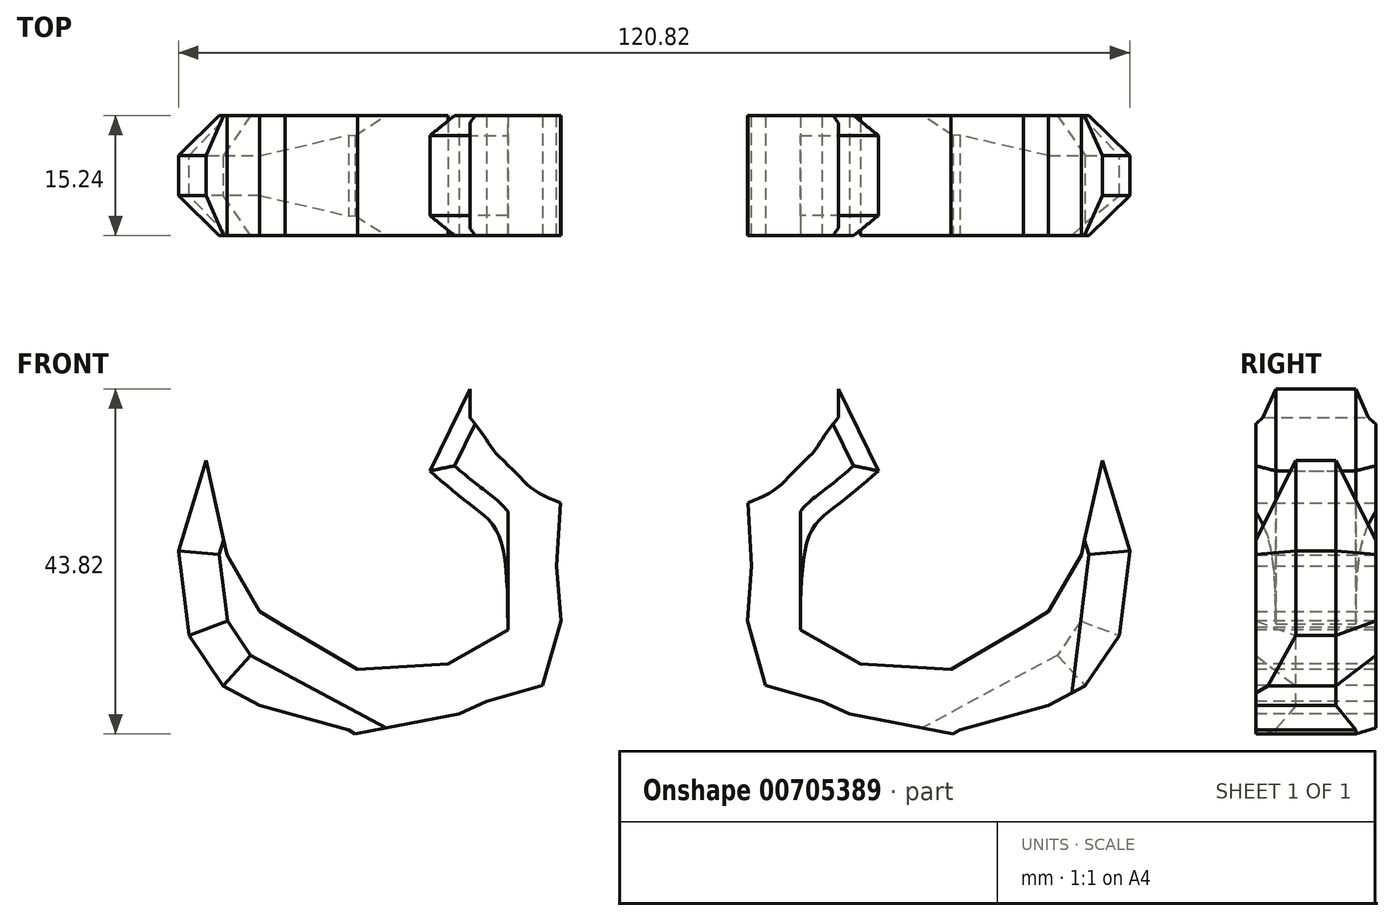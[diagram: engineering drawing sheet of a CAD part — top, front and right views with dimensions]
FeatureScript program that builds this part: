
annotation { "Feature Type Name" : "Feature", "Feature Type Description" : "" }
export const myFeature = defineFeature(function(context is Context, id is Id, definition is map)
    precondition{}
    {
        {
            var Q0;
            Q0=qCreatedBy(makeId("Front.planeOp"),FACE);
            var sketch = newSketch(context, id + "F0", { "sketchPlane" : qUnion([Q0])});
            skLineSegment(sketch, "E0", {"start": v(0, 0) * mm, "end": v(0, -3.04) * mm});
            skLineSegment(sketch, "E1", {"start": v(0, -3.04) * mm, "end": v(0, 0) * mm});
            skLineSegment(sketch, "E2", {"start": v(0, 15.49) * mm, "end": v(-8.28, 1.23) * mm});
            skLineSegment(sketch, "E3", {"start": v(-8.28, 1.23) * mm, "end": v(-12.37, 8.16) * mm});
            skLineSegment(sketch, "E4", {"start": v(-12.37, 8.16) * mm, "end": v(-11.9, 16.15) * mm});
            skFitSpline(sketch, "E5", {"points": [v(-11.9, 16.15) * mm, v(-15.37, 17.85) * mm, v(-17.68, 20.08) * mm, v(-20.4, 22.8) * mm, v(-21.58, 24.61) * mm, v(-23.4, 26.98) * mm], "startDerivative": vector(-17.13, 6.88) * mm, "endDerivative": vector(-10.36, 12.7) * mm});
            skLineSegment(sketch, "E6", {"start": v(-23.4, 26.98) * mm, "end": v(-23.4, 30.61) * mm});
            skLineSegment(sketch, "E7", {"start": v(-23.4, 30.61) * mm, "end": v(-28.49, 20.22) * mm});
            skFitSpline(sketch, "E8", {"points": [v(-28.49, 20.22) * mm, v(-23.37, 15.92) * mm, v(-19.88, 12.37) * mm, v(-18.57, 0.8) * mm], "startDerivative": vector(16.73, -14.68) * mm, "endDerivative": vector(0.35, -32.63) * mm});
            skLineSegment(sketch, "E9", {"start": v(-18.57, 0.8) * mm, "end": v(-25.11, 4.23) * mm});
            skFitSpline(sketch, "E10", {"points": [v(-25.11, 4.23) * mm, v(-32.14, 3.58) * mm, v(-37.97, 4.1) * mm, v(-37.97, 4.11) * mm, v(-37.98, 4.1) * mm], "startDerivative": vector(-12.52, -2.08) * mm, "endDerivative": vector(-0.69, -0.74) * mm});
            skLineSegment(sketch, "E11", {"start": v(-37.97, 4.11) * mm, "end": v(-43.4, 7.41) * mm});
            skLineSegment(sketch, "E12", {"start": v(-43.4, 7.41) * mm, "end": v(-46.92, 12.83) * mm});
            skLineSegment(sketch, "E13", {"start": v(-46.92, 12.83) * mm, "end": v(-48.7, 6.64) * mm});
            skLineSegment(sketch, "E14", {"start": v(-48.7, 6.64) * mm, "end": v(-46.89, 0.36) * mm});
            skLineSegment(sketch, "E15", {"start": v(-46.89, 0.36) * mm, "end": v(-50.1, 2.34) * mm});
            skLineSegment(sketch, "E16", {"start": v(-50.1, 2.34) * mm, "end": v(-54.25, 9.51) * mm});
            skLineSegment(sketch, "E17", {"start": v(-54.25, 9.51) * mm, "end": v(-56.92, 21.51) * mm});
            skLineSegment(sketch, "E18", {"start": v(-56.92, 21.51) * mm, "end": v(-60.41, 10.04) * mm});
            skLineSegment(sketch, "E19", {"start": v(-60.41, 10.04) * mm, "end": v(-59.08, -0.72) * mm});
            skLineSegment(sketch, "E20", {"start": v(-59.08, -0.72) * mm, "end": v(-61.47, 1.15) * mm});
            skLineSegment(sketch, "E21", {"start": v(-61.47, 1.15) * mm, "end": v(-65.53, 8.08) * mm});
            skLineSegment(sketch, "E22", {"start": v(-65.53, 8.08) * mm, "end": v(-66.84, 23.61) * mm});
            skLineSegment(sketch, "E23", {"start": v(-66.84, 23.61) * mm, "end": v(-70.54, 10.04) * mm});
            skLineSegment(sketch, "E24", {"start": v(-70.54, 10.04) * mm, "end": v(-70.54, -4.38) * mm});
            skLineSegment(sketch, "E25", {"start": v(-70.54, -4.38) * mm, "end": v(-64.04, -13.92) * mm});
            skLineSegment(sketch, "E26", {"start": v(-64.04, -13.92) * mm, "end": v(-58.26, -17.24) * mm});
            skLineSegment(sketch, "E27", {"start": v(-58.26, -17.24) * mm, "end": v(-57.47, -21.38) * mm});
            skLineSegment(sketch, "E28", {"start": v(-57.47, -21.38) * mm, "end": v(-50, -19.34) * mm});
            skLineSegment(sketch, "E29", {"start": v(-50, -19.34) * mm, "end": v(-43.4, -18.73) * mm});
            skLineSegment(sketch, "E30", {"start": v(-43.4, -18.73) * mm, "end": v(-31.64, -30.05) * mm});
            skLineSegment(sketch, "E31", {"start": v(-31.64, -30.05) * mm, "end": v(-30.93, -21.53) * mm});
            skLineSegment(sketch, "E32", {"start": v(-30.93, -21.53) * mm, "end": v(-24.8, -15.98) * mm});
            skLineSegment(sketch, "E33", {"start": v(-24.8, -15.98) * mm, "end": v(-12.45, -11.17) * mm});
            skLineSegment(sketch, "E34", {"start": v(-12.45, -11.17) * mm, "end": v(-2.8, -10.37) * mm});
            skLineSegment(sketch, "E35", {"start": v(-2.8, -10.37) * mm, "end": v(0, -15.23) * mm});
            skLineSegment(sketch, "E36", {"start": v(0, -15.23) * mm, "end": v(-2.8, -10.37) * mm});
            skLineSegment(sketch, "E37.MirrorCS", {"start": v(0, 15.49) * mm, "end": v(8.28, 1.23) * mm});
            skLineSegment(sketch, "E38.MirrorCS", {"start": v(0, -15.23) * mm, "end": v(2.8, -10.37) * mm});
            skLineSegment(sketch, "E39.MirrorCS", {"start": v(12.45, -11.17) * mm, "end": v(2.8, -10.37) * mm});
            skLineSegment(sketch, "E40.MirrorCS", {"start": v(8.28, 1.23) * mm, "end": v(12.37, 8.16) * mm});
            skLineSegment(sketch, "E41.MirrorCS", {"start": v(12.37, 8.16) * mm, "end": v(11.9, 16.15) * mm});
            skFitSpline(sketch, "E42.MirrorCS", {"points": [v(11.9, 16.15) * mm, v(15.37, 17.85) * mm, v(17.68, 20.08) * mm, v(20.4, 22.8) * mm, v(21.58, 24.61) * mm, v(23.4, 26.98) * mm], "startDerivative": vector(17.13, 6.88) * mm, "endDerivative": vector(10.36, 12.7) * mm});
            skLineSegment(sketch, "E43.MirrorCS", {"start": v(23.4, 30.61) * mm, "end": v(28.49, 20.22) * mm});
            skLineSegment(sketch, "E44.MirrorCS", {"start": v(23.4, 26.98) * mm, "end": v(23.4, 30.61) * mm});
            skFitSpline(sketch, "E45.MirrorCS", {"points": [v(28.49, 20.22) * mm, v(23.37, 15.92) * mm, v(19.88, 12.37) * mm, v(18.57, 0.8) * mm], "startDerivative": vector(-16.73, -14.68) * mm, "endDerivative": vector(-0.35, -32.63) * mm});
            skLineSegment(sketch, "E46.MirrorCS", {"start": v(18.57, 0.8) * mm, "end": v(25.11, 4.23) * mm});
            skFitSpline(sketch, "E47.MirrorCS", {"points": [v(25.11, 4.23) * mm, v(32.14, 3.58) * mm, v(37.97, 4.1) * mm, v(37.97, 4.11) * mm, v(37.98, 4.1) * mm], "startDerivative": vector(12.52, -2.08) * mm, "endDerivative": vector(0.69, -0.74) * mm});
            skLineSegment(sketch, "E48.MirrorCS", {"start": v(37.97, 4.11) * mm, "end": v(43.4, 7.41) * mm});
            skLineSegment(sketch, "E49.MirrorCS", {"start": v(43.4, 7.41) * mm, "end": v(46.92, 12.83) * mm});
            skLineSegment(sketch, "E50.MirrorCS", {"start": v(46.92, 12.83) * mm, "end": v(48.7, 6.64) * mm});
            skLineSegment(sketch, "E51.MirrorCS", {"start": v(48.7, 6.64) * mm, "end": v(46.89, 0.36) * mm});
            skLineSegment(sketch, "E52.MirrorCS", {"start": v(46.89, 0.36) * mm, "end": v(50.1, 2.34) * mm});
            skLineSegment(sketch, "E53.MirrorCS", {"start": v(50.1, 2.34) * mm, "end": v(54.25, 9.51) * mm});
            skLineSegment(sketch, "E54.MirrorCS", {"start": v(54.25, 9.51) * mm, "end": v(56.92, 21.51) * mm});
            skLineSegment(sketch, "E55.MirrorCS", {"start": v(56.92, 21.51) * mm, "end": v(60.41, 10.04) * mm});
            skLineSegment(sketch, "E56.MirrorCS", {"start": v(60.41, 10.04) * mm, "end": v(59.08, -0.72) * mm});
            skLineSegment(sketch, "E57.MirrorCS", {"start": v(59.08, -0.72) * mm, "end": v(61.47, 1.15) * mm});
            skLineSegment(sketch, "E58.MirrorCS", {"start": v(61.47, 1.15) * mm, "end": v(65.53, 8.08) * mm});
            skLineSegment(sketch, "E59.MirrorCS", {"start": v(65.53, 8.08) * mm, "end": v(66.84, 23.61) * mm});
            skLineSegment(sketch, "E60.MirrorCS", {"start": v(66.84, 23.61) * mm, "end": v(70.54, 10.04) * mm});
            skLineSegment(sketch, "E61.MirrorCS", {"start": v(70.54, 10.04) * mm, "end": v(70.54, -4.38) * mm});
            skLineSegment(sketch, "E62.MirrorCS", {"start": v(70.54, -4.38) * mm, "end": v(64.04, -13.92) * mm});
            skLineSegment(sketch, "E63.MirrorCS", {"start": v(64.04, -13.92) * mm, "end": v(58.26, -17.24) * mm});
            skLineSegment(sketch, "E64.MirrorCS", {"start": v(58.26, -17.24) * mm, "end": v(57.47, -21.38) * mm});
            skLineSegment(sketch, "E65.MirrorCS", {"start": v(57.47, -21.38) * mm, "end": v(50, -19.34) * mm});
            skLineSegment(sketch, "E66.MirrorCS", {"start": v(50, -19.34) * mm, "end": v(43.4, -18.73) * mm});
            skLineSegment(sketch, "E67.MirrorCS", {"start": v(43.4, -18.73) * mm, "end": v(31.64, -30.05) * mm});
            skLineSegment(sketch, "E68.MirrorCS", {"start": v(31.64, -30.05) * mm, "end": v(30.93, -21.53) * mm});
            skLineSegment(sketch, "E69.MirrorCS", {"start": v(30.93, -21.53) * mm, "end": v(24.8, -15.98) * mm});
            skLineSegment(sketch, "E70.MirrorCS", {"start": v(24.8, -15.98) * mm, "end": v(12.45, -11.17) * mm});
            skSolve(sketch);
        }
        {
            var Q0;
            Q0=makeQuery(id+"F0.imprint","IMPRINT",FACE,{"disambiguationData":[TD([[makeQuery(id+"F0.imprint","IMPRINT",EDGE,{"derivedFrom":sQuery(id+"F0.wireOp",EDGE,"E2")}),1.0]])]});
            extrude(context, id + "F1", {"entities" : qUnion([Q0]), "depth" : 7.62 * mm, "offsetDistance" : 25.4 * mm});
        }
        {
            var Q0;
            Q0=makeQuery(id+"F1.opExtrude","CAP_FACE",FACE,{"disambiguationData":[OSD([sQuery(id+"F0.wireOp",EDGE,"E2"),sQuery(id+"F0.wireOp",EDGE,"E3"),sQuery(id+"F0.wireOp",EDGE,"E4"),sQuery(id+"F0.wireOp",EDGE,"E5"),sQuery(id+"F0.wireOp",EDGE,"E6"),sQuery(id+"F0.wireOp",EDGE,"E7"),sQuery(id+"F0.wireOp",EDGE,"E8"),sQuery(id+"F0.wireOp",EDGE,"E9"),sQuery(id+"F0.wireOp",EDGE,"E10"),sQuery(id+"F0.wireOp",EDGE,"E11"),sQuery(id+"F0.wireOp",EDGE,"E12"),sQuery(id+"F0.wireOp",EDGE,"E13"),sQuery(id+"F0.wireOp",EDGE,"E14"),sQuery(id+"F0.wireOp",EDGE,"E15"),sQuery(id+"F0.wireOp",EDGE,"E16"),sQuery(id+"F0.wireOp",EDGE,"E17"),sQuery(id+"F0.wireOp",EDGE,"E18"),sQuery(id+"F0.wireOp",EDGE,"E19"),sQuery(id+"F0.wireOp",EDGE,"E20"),sQuery(id+"F0.wireOp",EDGE,"E21"),sQuery(id+"F0.wireOp",EDGE,"E22"),sQuery(id+"F0.wireOp",EDGE,"E23"),sQuery(id+"F0.wireOp",EDGE,"E24"),sQuery(id+"F0.wireOp",EDGE,"E25"),sQuery(id+"F0.wireOp",EDGE,"E26"),sQuery(id+"F0.wireOp",EDGE,"E27"),sQuery(id+"F0.wireOp",EDGE,"E28"),sQuery(id+"F0.wireOp",EDGE,"E29"),sQuery(id+"F0.wireOp",EDGE,"E30"),sQuery(id+"F0.wireOp",EDGE,"E31"),sQuery(id+"F0.wireOp",EDGE,"E32"),sQuery(id+"F0.wireOp",EDGE,"E33"),sQuery(id+"F0.wireOp",EDGE,"E34"),sQuery(id+"F0.wireOp",EDGE,"E36"),sQuery(id+"F0.wireOp",EDGE,"E37.MirrorCS"),sQuery(id+"F0.wireOp",EDGE,"E38.MirrorCS"),sQuery(id+"F0.wireOp",EDGE,"E39.MirrorCS"),sQuery(id+"F0.wireOp",EDGE,"E40.MirrorCS"),sQuery(id+"F0.wireOp",EDGE,"E41.MirrorCS"),sQuery(id+"F0.wireOp",EDGE,"E42.MirrorCS"),sQuery(id+"F0.wireOp",EDGE,"E43.MirrorCS"),sQuery(id+"F0.wireOp",EDGE,"E44.MirrorCS"),sQuery(id+"F0.wireOp",EDGE,"E45.MirrorCS"),sQuery(id+"F0.wireOp",EDGE,"E46.MirrorCS"),sQuery(id+"F0.wireOp",EDGE,"E47.MirrorCS"),sQuery(id+"F0.wireOp",EDGE,"E48.MirrorCS"),sQuery(id+"F0.wireOp",EDGE,"E49.MirrorCS"),sQuery(id+"F0.wireOp",EDGE,"E50.MirrorCS"),sQuery(id+"F0.wireOp",EDGE,"E51.MirrorCS"),sQuery(id+"F0.wireOp",EDGE,"E52.MirrorCS"),sQuery(id+"F0.wireOp",EDGE,"E53.MirrorCS"),sQuery(id+"F0.wireOp",EDGE,"E54.MirrorCS"),sQuery(id+"F0.wireOp",EDGE,"E55.MirrorCS"),sQuery(id+"F0.wireOp",EDGE,"E56.MirrorCS"),sQuery(id+"F0.wireOp",EDGE,"E57.MirrorCS"),sQuery(id+"F0.wireOp",EDGE,"E58.MirrorCS"),sQuery(id+"F0.wireOp",EDGE,"E59.MirrorCS"),sQuery(id+"F0.wireOp",EDGE,"E60.MirrorCS"),sQuery(id+"F0.wireOp",EDGE,"E61.MirrorCS"),sQuery(id+"F0.wireOp",EDGE,"E62.MirrorCS"),sQuery(id+"F0.wireOp",EDGE,"E63.MirrorCS"),sQuery(id+"F0.wireOp",EDGE,"E64.MirrorCS"),sQuery(id+"F0.wireOp",EDGE,"E65.MirrorCS"),sQuery(id+"F0.wireOp",EDGE,"E66.MirrorCS"),sQuery(id+"F0.wireOp",EDGE,"E67.MirrorCS"),sQuery(id+"F0.wireOp",EDGE,"E68.MirrorCS"),sQuery(id+"F0.wireOp",EDGE,"E69.MirrorCS"),sQuery(id+"F0.wireOp",EDGE,"E70.MirrorCS")])],"isStart":true});
            extrude(context, id + "F2", {"entities" : qUnion([Q0]), "operationType" : NewBodyOperationType.ADD, "depth" : 7.62 * mm, "offsetDistance" : 25.4 * mm});
        }
        {
            var Q0;
            Q0=makeQuery(id+"F1.opExtrude","CAP_FACE",FACE,{"disambiguationData":[OSD([sQuery(id+"F0.wireOp",EDGE,"E2"),sQuery(id+"F0.wireOp",EDGE,"E3"),sQuery(id+"F0.wireOp",EDGE,"E4"),sQuery(id+"F0.wireOp",EDGE,"E5"),sQuery(id+"F0.wireOp",EDGE,"E6"),sQuery(id+"F0.wireOp",EDGE,"E7"),sQuery(id+"F0.wireOp",EDGE,"E8"),sQuery(id+"F0.wireOp",EDGE,"E9"),sQuery(id+"F0.wireOp",EDGE,"E10"),sQuery(id+"F0.wireOp",EDGE,"E11"),sQuery(id+"F0.wireOp",EDGE,"E12"),sQuery(id+"F0.wireOp",EDGE,"E13"),sQuery(id+"F0.wireOp",EDGE,"E14"),sQuery(id+"F0.wireOp",EDGE,"E15"),sQuery(id+"F0.wireOp",EDGE,"E16"),sQuery(id+"F0.wireOp",EDGE,"E17"),sQuery(id+"F0.wireOp",EDGE,"E18"),sQuery(id+"F0.wireOp",EDGE,"E19"),sQuery(id+"F0.wireOp",EDGE,"E20"),sQuery(id+"F0.wireOp",EDGE,"E21"),sQuery(id+"F0.wireOp",EDGE,"E22"),sQuery(id+"F0.wireOp",EDGE,"E23"),sQuery(id+"F0.wireOp",EDGE,"E24"),sQuery(id+"F0.wireOp",EDGE,"E25"),sQuery(id+"F0.wireOp",EDGE,"E26"),sQuery(id+"F0.wireOp",EDGE,"E27"),sQuery(id+"F0.wireOp",EDGE,"E28"),sQuery(id+"F0.wireOp",EDGE,"E29"),sQuery(id+"F0.wireOp",EDGE,"E30"),sQuery(id+"F0.wireOp",EDGE,"E31"),sQuery(id+"F0.wireOp",EDGE,"E32"),sQuery(id+"F0.wireOp",EDGE,"E33"),sQuery(id+"F0.wireOp",EDGE,"E34"),sQuery(id+"F0.wireOp",EDGE,"E36"),sQuery(id+"F0.wireOp",EDGE,"E37.MirrorCS"),sQuery(id+"F0.wireOp",EDGE,"E38.MirrorCS"),sQuery(id+"F0.wireOp",EDGE,"E39.MirrorCS"),sQuery(id+"F0.wireOp",EDGE,"E40.MirrorCS"),sQuery(id+"F0.wireOp",EDGE,"E41.MirrorCS"),sQuery(id+"F0.wireOp",EDGE,"E42.MirrorCS"),sQuery(id+"F0.wireOp",EDGE,"E43.MirrorCS"),sQuery(id+"F0.wireOp",EDGE,"E44.MirrorCS"),sQuery(id+"F0.wireOp",EDGE,"E45.MirrorCS"),sQuery(id+"F0.wireOp",EDGE,"E46.MirrorCS"),sQuery(id+"F0.wireOp",EDGE,"E47.MirrorCS"),sQuery(id+"F0.wireOp",EDGE,"E48.MirrorCS"),sQuery(id+"F0.wireOp",EDGE,"E49.MirrorCS"),sQuery(id+"F0.wireOp",EDGE,"E50.MirrorCS"),sQuery(id+"F0.wireOp",EDGE,"E51.MirrorCS"),sQuery(id+"F0.wireOp",EDGE,"E52.MirrorCS"),sQuery(id+"F0.wireOp",EDGE,"E53.MirrorCS"),sQuery(id+"F0.wireOp",EDGE,"E54.MirrorCS"),sQuery(id+"F0.wireOp",EDGE,"E55.MirrorCS"),sQuery(id+"F0.wireOp",EDGE,"E56.MirrorCS"),sQuery(id+"F0.wireOp",EDGE,"E57.MirrorCS"),sQuery(id+"F0.wireOp",EDGE,"E58.MirrorCS"),sQuery(id+"F0.wireOp",EDGE,"E59.MirrorCS"),sQuery(id+"F0.wireOp",EDGE,"E60.MirrorCS"),sQuery(id+"F0.wireOp",EDGE,"E61.MirrorCS"),sQuery(id+"F0.wireOp",EDGE,"E62.MirrorCS"),sQuery(id+"F0.wireOp",EDGE,"E63.MirrorCS"),sQuery(id+"F0.wireOp",EDGE,"E64.MirrorCS"),sQuery(id+"F0.wireOp",EDGE,"E65.MirrorCS"),sQuery(id+"F0.wireOp",EDGE,"E66.MirrorCS"),sQuery(id+"F0.wireOp",EDGE,"E67.MirrorCS"),sQuery(id+"F0.wireOp",EDGE,"E68.MirrorCS"),sQuery(id+"F0.wireOp",EDGE,"E69.MirrorCS"),sQuery(id+"F0.wireOp",EDGE,"E70.MirrorCS")])],"isStart":false});
            var sketch = newSketch(context, id + "F3", { "sketchPlane" : qUnion([Q0])});
            skLineSegment(sketch, "E71", {"start": v(46.89, 0.36) * mm, "end": v(37.7, -5.04) * mm});
            skLineSegment(sketch, "E72", {"start": v(37.7, -5.04) * mm, "end": v(26.18, -4.3) * mm});
            skLineSegment(sketch, "E73", {"start": v(26.18, -4.3) * mm, "end": v(18.57, 0) * mm});
            skLineSegment(sketch, "E74", {"start": v(18.57, 0) * mm, "end": v(18.57, 0.8) * mm});
            skLineSegment(sketch, "E75", {"start": v(18.57, 0.8) * mm, "end": v(18.57, 0) * mm});
            skLineSegment(sketch, "E76", {"start": v(59.08, -0.72) * mm, "end": v(54.73, -7.1) * mm});
            skLineSegment(sketch, "E77", {"start": v(54.73, -7.1) * mm, "end": v(50.1, -9.58) * mm});
            skLineSegment(sketch, "E78", {"start": v(50.1, -9.58) * mm, "end": v(38.82, -12.7) * mm});
            skLineSegment(sketch, "E79", {"start": v(38.82, -12.7) * mm, "end": v(37.97, -13.2) * mm});
            skLineSegment(sketch, "E80", {"start": v(37.97, -13.2) * mm, "end": v(24.78, -10.64) * mm});
            skLineSegment(sketch, "E81", {"start": v(24.78, -10.64) * mm, "end": v(21.3, -9.07) * mm});
            skLineSegment(sketch, "E82", {"start": v(21.3, -9.07) * mm, "end": v(14.16, -7.03) * mm});
            skLineSegment(sketch, "E83", {"start": v(14.16, -7.03) * mm, "end": v(11.83, 1.15) * mm});
            skLineSegment(sketch, "E84", {"start": v(11.83, 1.15) * mm, "end": v(12.37, 8.16) * mm});
            skLineSegment(sketch, "E85", {"start": v(8.28, 1.23) * mm, "end": v(9, 0) * mm});
            skLineSegment(sketch, "E86", {"start": v(9, 0) * mm, "end": v(2.8, -10.37) * mm});
            skLineSegment(sketch, "E87", {"start": v(2.8, -10.37) * mm, "end": v(9, 0) * mm});
            skLineSegment(sketch, "E88", {"start": v(0, 0) * mm, "end": v(0, -1.55) * mm});
            skLineSegment(sketch, "E89", {"start": v(0, -1.55) * mm, "end": v(0, 0) * mm});
            skLineSegment(sketch, "E90.MirrorCS", {"start": v(-2.8, -10.37) * mm, "end": v(-9, 0) * mm});
            skLineSegment(sketch, "E91.MirrorCS", {"start": v(-8.28, 1.23) * mm, "end": v(-9, 0) * mm});
            skLineSegment(sketch, "E92.MirrorCS", {"start": v(-11.83, 1.15) * mm, "end": v(-12.37, 8.16) * mm});
            skLineSegment(sketch, "E93.MirrorCS", {"start": v(-14.16, -7.03) * mm, "end": v(-11.83, 1.15) * mm});
            skLineSegment(sketch, "E94.MirrorCS", {"start": v(-21.3, -9.07) * mm, "end": v(-14.16, -7.03) * mm});
            skLineSegment(sketch, "E95.MirrorCS", {"start": v(-24.78, -10.64) * mm, "end": v(-21.3, -9.07) * mm});
            skLineSegment(sketch, "E96.MirrorCS", {"start": v(-37.97, -13.2) * mm, "end": v(-24.78, -10.64) * mm});
            skLineSegment(sketch, "E97.MirrorCS", {"start": v(-50.1, -9.58) * mm, "end": v(-38.82, -12.7) * mm});
            skLineSegment(sketch, "E98.MirrorCS", {"start": v(-38.82, -12.7) * mm, "end": v(-37.97, -13.2) * mm});
            skLineSegment(sketch, "E99.MirrorCS", {"start": v(-54.73, -7.1) * mm, "end": v(-50.1, -9.58) * mm});
            skLineSegment(sketch, "E100.MirrorCS", {"start": v(-59.08, -0.72) * mm, "end": v(-54.73, -7.1) * mm});
            skLineSegment(sketch, "E101.MirrorCS", {"start": v(-46.89, 0.36) * mm, "end": v(-37.7, -5.04) * mm});
            skLineSegment(sketch, "E102.MirrorCS", {"start": v(-37.7, -5.04) * mm, "end": v(-26.18, -4.3) * mm});
            skLineSegment(sketch, "E103.MirrorCS", {"start": v(-26.18, -4.3) * mm, "end": v(-18.57, 0) * mm});
            skLineSegment(sketch, "E104.MirrorCS", {"start": v(-18.57, 0.8) * mm, "end": v(-18.57, 0) * mm});
            skSolve(sketch);
        }
        {
            var Q0;
            Q0=makeQuery(id+"F3.imprint","IMPRINT",FACE,{"disambiguationData":[TD([[makeQuery(id+"F3.imprint","IMPRINT",EDGE,{"derivedFrom":sQuery(id+"F3.wireOp",EDGE,"E71")}),-1.0]])]});
            var Q1;
            Q1=makeQuery(id+"F3.imprint","IMPRINT",FACE,{"disambiguationData":[TD([[makeQuery(id+"F3.imprint","IMPRINT",EDGE,{"derivedFrom":sQuery(id+"F3.wireOp",EDGE,"E76")}),1.0]])]});
            var Q2;
            Q2=makeQuery(id+"F3.imprint","IMPRINT",FACE,{"disambiguationData":[TD([[makeQuery(id+"F3.imprint","IMPRINT",EDGE,{"derivedFrom":sQuery(id+"F3.wireOp",EDGE,"E85")}),-1.0]])]});
            var Q3;
            Q3=makeQuery(id+"F3.imprint","IMPRINT",FACE,{"disambiguationData":[TD([[makeQuery(id+"F3.imprint","IMPRINT",EDGE,{"derivedFrom":sQuery(id+"F3.wireOp",EDGE,"E90.MirrorCS")}),1.0]])]});
            var Q4;
            Q4=makeQuery(id+"F3.imprint","IMPRINT",FACE,{"disambiguationData":[TD([[makeQuery(id+"F3.imprint","IMPRINT",EDGE,{"derivedFrom":sQuery(id+"F3.wireOp",EDGE,"E101.MirrorCS")}),1.0]])]});
            extrude(context, id + "F4", {"entities" : qUnion([Q0, Q1, Q2, Q3, Q4]), "operationType" : NewBodyOperationType.REMOVE, "oppositeDirection" : true, "depth" : 25.4 * mm, "offsetDistance" : 25.4 * mm});
        }
        {
            var Q0;
            Q0=makeQuery(id+"F1.opExtrude","CAP_EDGE",EDGE,{"disambiguationData":[OSD([sQuery(id+"F0.wireOp",EDGE,"E55.MirrorCS")])],"isStart":false});
            var Q1;
            Q1=makeQuery(id+"F1.opExtrude","CAP_EDGE",EDGE,{"disambiguationData":[OSD([sQuery(id+"F0.wireOp",EDGE,"E56.MirrorCS")])],"isStart":false});
            var Q2;
            Q2=makeQuery(id+"F4.boolean.opBoolean","COPY",EDGE,{"derivedFrom":makeQuery(id+"F4.opExtrude","CAP_EDGE",EDGE,{"disambiguationData":[OSD([sQuery(id+"F3.wireOp",EDGE,"E76")])],"isStart":true})});
            var Q3;
            Q3=makeQuery(id+"F4.boolean.opBoolean","COPY",EDGE,{"derivedFrom":makeQuery(id+"F4.opExtrude","CAP_EDGE",EDGE,{"disambiguationData":[OSD([sQuery(id+"F3.wireOp",EDGE,"E77")])],"isStart":true})});
            var Q4;
            Q4=makeQuery(id+"F4.boolean.opBoolean","COPY",EDGE,{"derivedFrom":makeQuery(id+"F4.opExtrude","CAP_EDGE",EDGE,{"disambiguationData":[OSD([sQuery(id+"F3.wireOp",EDGE,"E99.MirrorCS")])],"isStart":true})});
            var Q5;
            Q5=makeQuery(id+"F4.boolean.opBoolean","COPY",EDGE,{"derivedFrom":makeQuery(id+"F4.opExtrude","CAP_EDGE",EDGE,{"disambiguationData":[OSD([sQuery(id+"F3.wireOp",EDGE,"E100.MirrorCS")])],"isStart":true})});
            var Q6;
            Q6=makeQuery(id+"F1.opExtrude","CAP_EDGE",EDGE,{"disambiguationData":[OSD([sQuery(id+"F0.wireOp",EDGE,"E19")])],"isStart":false});
            var Q7;
            Q7=makeQuery(id+"F1.opExtrude","CAP_EDGE",EDGE,{"disambiguationData":[OSD([sQuery(id+"F0.wireOp",EDGE,"E18")])],"isStart":false});
            var Q8;
            Q8=makeQuery(id+"F4.boolean.opBoolean","COPY",EDGE,{"derivedFrom":makeQuery(id+"F4.opExtrude","CAP_EDGE",EDGE,{"disambiguationData":[OSD([sQuery(id+"F3.wireOp",EDGE,"E99.MirrorCS")])],"isStart":false})});
            var Q9;
            Q9=makeQuery(id+"F4.boolean.opBoolean","COPY",EDGE,{"derivedFrom":makeQuery(id+"F4.opExtrude","CAP_EDGE",EDGE,{"disambiguationData":[OSD([sQuery(id+"F3.wireOp",EDGE,"E100.MirrorCS")])],"isStart":false})});
            var Q10;
            Q10=makeQuery(id+"F2.opExtrude","CAP_EDGE",EDGE,{"disambiguationData":[OSD([sQuery(id+"F0.wireOp",EDGE,"E19")])],"isStart":false});
            var Q11;
            Q11=makeQuery(id+"F2.opExtrude","CAP_EDGE",EDGE,{"disambiguationData":[OSD([sQuery(id+"F0.wireOp",EDGE,"E18")])],"isStart":false});
            var Q12;
            Q12=makeQuery(id+"F4.boolean.opBoolean","COPY",EDGE,{"derivedFrom":makeQuery(id+"F4.opExtrude","CAP_EDGE",EDGE,{"disambiguationData":[OSD([sQuery(id+"F3.wireOp",EDGE,"E77")])],"isStart":false})});
            var Q13;
            Q13=makeQuery(id+"F4.boolean.opBoolean","COPY",EDGE,{"derivedFrom":makeQuery(id+"F4.opExtrude","CAP_EDGE",EDGE,{"disambiguationData":[OSD([sQuery(id+"F3.wireOp",EDGE,"E76")])],"isStart":false})});
            var Q14;
            Q14=makeQuery(id+"F2.opExtrude","CAP_EDGE",EDGE,{"disambiguationData":[OSD([sQuery(id+"F0.wireOp",EDGE,"E56.MirrorCS")])],"isStart":false});
            var Q15;
            Q15=makeQuery(id+"F2.opExtrude","CAP_EDGE",EDGE,{"disambiguationData":[OSD([sQuery(id+"F0.wireOp",EDGE,"E55.MirrorCS")])],"isStart":false});
            var Q16;
            Q16=makeQuery(id+"F4.boolean.opBoolean","INTERSECT",EDGE,{"derivedFrom":[makeQuery(id+"F2.opExtrude","CAP_FACE",FACE,{"disambiguationData":[OSD([sQuery(id+"F0.wireOp",EDGE,"E2"),sQuery(id+"F0.wireOp",EDGE,"E3"),sQuery(id+"F0.wireOp",EDGE,"E4"),sQuery(id+"F0.wireOp",EDGE,"E5"),sQuery(id+"F0.wireOp",EDGE,"E6"),sQuery(id+"F0.wireOp",EDGE,"E7"),sQuery(id+"F0.wireOp",EDGE,"E8"),sQuery(id+"F0.wireOp",EDGE,"E9"),sQuery(id+"F0.wireOp",EDGE,"E10"),sQuery(id+"F0.wireOp",EDGE,"E11"),sQuery(id+"F0.wireOp",EDGE,"E12"),sQuery(id+"F0.wireOp",EDGE,"E13"),sQuery(id+"F0.wireOp",EDGE,"E14"),sQuery(id+"F0.wireOp",EDGE,"E15"),sQuery(id+"F0.wireOp",EDGE,"E16"),sQuery(id+"F0.wireOp",EDGE,"E17"),sQuery(id+"F0.wireOp",EDGE,"E18"),sQuery(id+"F0.wireOp",EDGE,"E19"),sQuery(id+"F0.wireOp",EDGE,"E20"),sQuery(id+"F0.wireOp",EDGE,"E21"),sQuery(id+"F0.wireOp",EDGE,"E22"),sQuery(id+"F0.wireOp",EDGE,"E23"),sQuery(id+"F0.wireOp",EDGE,"E24"),sQuery(id+"F0.wireOp",EDGE,"E25"),sQuery(id+"F0.wireOp",EDGE,"E26"),sQuery(id+"F0.wireOp",EDGE,"E27"),sQuery(id+"F0.wireOp",EDGE,"E28"),sQuery(id+"F0.wireOp",EDGE,"E29"),sQuery(id+"F0.wireOp",EDGE,"E30"),sQuery(id+"F0.wireOp",EDGE,"E31"),sQuery(id+"F0.wireOp",EDGE,"E32"),sQuery(id+"F0.wireOp",EDGE,"E33"),sQuery(id+"F0.wireOp",EDGE,"E34"),sQuery(id+"F0.wireOp",EDGE,"E36"),sQuery(id+"F0.wireOp",EDGE,"E37.MirrorCS"),sQuery(id+"F0.wireOp",EDGE,"E38.MirrorCS"),sQuery(id+"F0.wireOp",EDGE,"E39.MirrorCS"),sQuery(id+"F0.wireOp",EDGE,"E40.MirrorCS"),sQuery(id+"F0.wireOp",EDGE,"E41.MirrorCS"),sQuery(id+"F0.wireOp",EDGE,"E42.MirrorCS"),sQuery(id+"F0.wireOp",EDGE,"E43.MirrorCS"),sQuery(id+"F0.wireOp",EDGE,"E44.MirrorCS"),sQuery(id+"F0.wireOp",EDGE,"E45.MirrorCS"),sQuery(id+"F0.wireOp",EDGE,"E46.MirrorCS"),sQuery(id+"F0.wireOp",EDGE,"E47.MirrorCS"),sQuery(id+"F0.wireOp",EDGE,"E48.MirrorCS"),sQuery(id+"F0.wireOp",EDGE,"E49.MirrorCS"),sQuery(id+"F0.wireOp",EDGE,"E50.MirrorCS"),sQuery(id+"F0.wireOp",EDGE,"E51.MirrorCS"),sQuery(id+"F0.wireOp",EDGE,"E52.MirrorCS"),sQuery(id+"F0.wireOp",EDGE,"E53.MirrorCS"),sQuery(id+"F0.wireOp",EDGE,"E54.MirrorCS"),sQuery(id+"F0.wireOp",EDGE,"E55.MirrorCS"),sQuery(id+"F0.wireOp",EDGE,"E56.MirrorCS"),sQuery(id+"F0.wireOp",EDGE,"E57.MirrorCS"),sQuery(id+"F0.wireOp",EDGE,"E58.MirrorCS"),sQuery(id+"F0.wireOp",EDGE,"E59.MirrorCS"),sQuery(id+"F0.wireOp",EDGE,"E60.MirrorCS"),sQuery(id+"F0.wireOp",EDGE,"E61.MirrorCS"),sQuery(id+"F0.wireOp",EDGE,"E62.MirrorCS"),sQuery(id+"F0.wireOp",EDGE,"E63.MirrorCS"),sQuery(id+"F0.wireOp",EDGE,"E64.MirrorCS"),sQuery(id+"F0.wireOp",EDGE,"E65.MirrorCS"),sQuery(id+"F0.wireOp",EDGE,"E66.MirrorCS"),sQuery(id+"F0.wireOp",EDGE,"E67.MirrorCS"),sQuery(id+"F0.wireOp",EDGE,"E68.MirrorCS"),sQuery(id+"F0.wireOp",EDGE,"E69.MirrorCS"),sQuery(id+"F0.wireOp",EDGE,"E70.MirrorCS")])],"isStart":false}),makeQuery(id+"F4.opExtrude","SWEPT_FACE",FACE,{"disambiguationData":[OSD([sQuery(id+"F3.wireOp",EDGE,"E77")])]})]});
            var Q17;
            Q17=makeQuery(id+"F4.boolean.opBoolean","INTERSECT",EDGE,{"derivedFrom":[makeQuery(id+"F2.opExtrude","CAP_FACE",FACE,{"disambiguationData":[OSD([sQuery(id+"F0.wireOp",EDGE,"E2"),sQuery(id+"F0.wireOp",EDGE,"E3"),sQuery(id+"F0.wireOp",EDGE,"E4"),sQuery(id+"F0.wireOp",EDGE,"E5"),sQuery(id+"F0.wireOp",EDGE,"E6"),sQuery(id+"F0.wireOp",EDGE,"E7"),sQuery(id+"F0.wireOp",EDGE,"E8"),sQuery(id+"F0.wireOp",EDGE,"E9"),sQuery(id+"F0.wireOp",EDGE,"E10"),sQuery(id+"F0.wireOp",EDGE,"E11"),sQuery(id+"F0.wireOp",EDGE,"E12"),sQuery(id+"F0.wireOp",EDGE,"E13"),sQuery(id+"F0.wireOp",EDGE,"E14"),sQuery(id+"F0.wireOp",EDGE,"E15"),sQuery(id+"F0.wireOp",EDGE,"E16"),sQuery(id+"F0.wireOp",EDGE,"E17"),sQuery(id+"F0.wireOp",EDGE,"E18"),sQuery(id+"F0.wireOp",EDGE,"E19"),sQuery(id+"F0.wireOp",EDGE,"E20"),sQuery(id+"F0.wireOp",EDGE,"E21"),sQuery(id+"F0.wireOp",EDGE,"E22"),sQuery(id+"F0.wireOp",EDGE,"E23"),sQuery(id+"F0.wireOp",EDGE,"E24"),sQuery(id+"F0.wireOp",EDGE,"E25"),sQuery(id+"F0.wireOp",EDGE,"E26"),sQuery(id+"F0.wireOp",EDGE,"E27"),sQuery(id+"F0.wireOp",EDGE,"E28"),sQuery(id+"F0.wireOp",EDGE,"E29"),sQuery(id+"F0.wireOp",EDGE,"E30"),sQuery(id+"F0.wireOp",EDGE,"E31"),sQuery(id+"F0.wireOp",EDGE,"E32"),sQuery(id+"F0.wireOp",EDGE,"E33"),sQuery(id+"F0.wireOp",EDGE,"E34"),sQuery(id+"F0.wireOp",EDGE,"E36"),sQuery(id+"F0.wireOp",EDGE,"E37.MirrorCS"),sQuery(id+"F0.wireOp",EDGE,"E38.MirrorCS"),sQuery(id+"F0.wireOp",EDGE,"E39.MirrorCS"),sQuery(id+"F0.wireOp",EDGE,"E40.MirrorCS"),sQuery(id+"F0.wireOp",EDGE,"E41.MirrorCS"),sQuery(id+"F0.wireOp",EDGE,"E42.MirrorCS"),sQuery(id+"F0.wireOp",EDGE,"E43.MirrorCS"),sQuery(id+"F0.wireOp",EDGE,"E44.MirrorCS"),sQuery(id+"F0.wireOp",EDGE,"E45.MirrorCS"),sQuery(id+"F0.wireOp",EDGE,"E46.MirrorCS"),sQuery(id+"F0.wireOp",EDGE,"E47.MirrorCS"),sQuery(id+"F0.wireOp",EDGE,"E48.MirrorCS"),sQuery(id+"F0.wireOp",EDGE,"E49.MirrorCS"),sQuery(id+"F0.wireOp",EDGE,"E50.MirrorCS"),sQuery(id+"F0.wireOp",EDGE,"E51.MirrorCS"),sQuery(id+"F0.wireOp",EDGE,"E52.MirrorCS"),sQuery(id+"F0.wireOp",EDGE,"E53.MirrorCS"),sQuery(id+"F0.wireOp",EDGE,"E54.MirrorCS"),sQuery(id+"F0.wireOp",EDGE,"E55.MirrorCS"),sQuery(id+"F0.wireOp",EDGE,"E56.MirrorCS"),sQuery(id+"F0.wireOp",EDGE,"E57.MirrorCS"),sQuery(id+"F0.wireOp",EDGE,"E58.MirrorCS"),sQuery(id+"F0.wireOp",EDGE,"E59.MirrorCS"),sQuery(id+"F0.wireOp",EDGE,"E60.MirrorCS"),sQuery(id+"F0.wireOp",EDGE,"E61.MirrorCS"),sQuery(id+"F0.wireOp",EDGE,"E62.MirrorCS"),sQuery(id+"F0.wireOp",EDGE,"E63.MirrorCS"),sQuery(id+"F0.wireOp",EDGE,"E64.MirrorCS"),sQuery(id+"F0.wireOp",EDGE,"E65.MirrorCS"),sQuery(id+"F0.wireOp",EDGE,"E66.MirrorCS"),sQuery(id+"F0.wireOp",EDGE,"E67.MirrorCS"),sQuery(id+"F0.wireOp",EDGE,"E68.MirrorCS"),sQuery(id+"F0.wireOp",EDGE,"E69.MirrorCS"),sQuery(id+"F0.wireOp",EDGE,"E70.MirrorCS")])],"isStart":false}),makeQuery(id+"F4.opExtrude","SWEPT_FACE",FACE,{"disambiguationData":[OSD([sQuery(id+"F3.wireOp",EDGE,"E76")])]})]});
            var Q18;
            Q18=makeQuery(id+"F4.boolean.opBoolean","INTERSECT",EDGE,{"derivedFrom":[makeQuery(id+"F2.opExtrude","CAP_FACE",FACE,{"disambiguationData":[OSD([sQuery(id+"F0.wireOp",EDGE,"E2"),sQuery(id+"F0.wireOp",EDGE,"E3"),sQuery(id+"F0.wireOp",EDGE,"E4"),sQuery(id+"F0.wireOp",EDGE,"E5"),sQuery(id+"F0.wireOp",EDGE,"E6"),sQuery(id+"F0.wireOp",EDGE,"E7"),sQuery(id+"F0.wireOp",EDGE,"E8"),sQuery(id+"F0.wireOp",EDGE,"E9"),sQuery(id+"F0.wireOp",EDGE,"E10"),sQuery(id+"F0.wireOp",EDGE,"E11"),sQuery(id+"F0.wireOp",EDGE,"E12"),sQuery(id+"F0.wireOp",EDGE,"E13"),sQuery(id+"F0.wireOp",EDGE,"E14"),sQuery(id+"F0.wireOp",EDGE,"E15"),sQuery(id+"F0.wireOp",EDGE,"E16"),sQuery(id+"F0.wireOp",EDGE,"E17"),sQuery(id+"F0.wireOp",EDGE,"E18"),sQuery(id+"F0.wireOp",EDGE,"E19"),sQuery(id+"F0.wireOp",EDGE,"E20"),sQuery(id+"F0.wireOp",EDGE,"E21"),sQuery(id+"F0.wireOp",EDGE,"E22"),sQuery(id+"F0.wireOp",EDGE,"E23"),sQuery(id+"F0.wireOp",EDGE,"E24"),sQuery(id+"F0.wireOp",EDGE,"E25"),sQuery(id+"F0.wireOp",EDGE,"E26"),sQuery(id+"F0.wireOp",EDGE,"E27"),sQuery(id+"F0.wireOp",EDGE,"E28"),sQuery(id+"F0.wireOp",EDGE,"E29"),sQuery(id+"F0.wireOp",EDGE,"E30"),sQuery(id+"F0.wireOp",EDGE,"E31"),sQuery(id+"F0.wireOp",EDGE,"E32"),sQuery(id+"F0.wireOp",EDGE,"E33"),sQuery(id+"F0.wireOp",EDGE,"E34"),sQuery(id+"F0.wireOp",EDGE,"E36"),sQuery(id+"F0.wireOp",EDGE,"E37.MirrorCS"),sQuery(id+"F0.wireOp",EDGE,"E38.MirrorCS"),sQuery(id+"F0.wireOp",EDGE,"E39.MirrorCS"),sQuery(id+"F0.wireOp",EDGE,"E40.MirrorCS"),sQuery(id+"F0.wireOp",EDGE,"E41.MirrorCS"),sQuery(id+"F0.wireOp",EDGE,"E42.MirrorCS"),sQuery(id+"F0.wireOp",EDGE,"E43.MirrorCS"),sQuery(id+"F0.wireOp",EDGE,"E44.MirrorCS"),sQuery(id+"F0.wireOp",EDGE,"E45.MirrorCS"),sQuery(id+"F0.wireOp",EDGE,"E46.MirrorCS"),sQuery(id+"F0.wireOp",EDGE,"E47.MirrorCS"),sQuery(id+"F0.wireOp",EDGE,"E48.MirrorCS"),sQuery(id+"F0.wireOp",EDGE,"E49.MirrorCS"),sQuery(id+"F0.wireOp",EDGE,"E50.MirrorCS"),sQuery(id+"F0.wireOp",EDGE,"E51.MirrorCS"),sQuery(id+"F0.wireOp",EDGE,"E52.MirrorCS"),sQuery(id+"F0.wireOp",EDGE,"E53.MirrorCS"),sQuery(id+"F0.wireOp",EDGE,"E54.MirrorCS"),sQuery(id+"F0.wireOp",EDGE,"E55.MirrorCS"),sQuery(id+"F0.wireOp",EDGE,"E56.MirrorCS"),sQuery(id+"F0.wireOp",EDGE,"E57.MirrorCS"),sQuery(id+"F0.wireOp",EDGE,"E58.MirrorCS"),sQuery(id+"F0.wireOp",EDGE,"E59.MirrorCS"),sQuery(id+"F0.wireOp",EDGE,"E60.MirrorCS"),sQuery(id+"F0.wireOp",EDGE,"E61.MirrorCS"),sQuery(id+"F0.wireOp",EDGE,"E62.MirrorCS"),sQuery(id+"F0.wireOp",EDGE,"E63.MirrorCS"),sQuery(id+"F0.wireOp",EDGE,"E64.MirrorCS"),sQuery(id+"F0.wireOp",EDGE,"E65.MirrorCS"),sQuery(id+"F0.wireOp",EDGE,"E66.MirrorCS"),sQuery(id+"F0.wireOp",EDGE,"E67.MirrorCS"),sQuery(id+"F0.wireOp",EDGE,"E68.MirrorCS"),sQuery(id+"F0.wireOp",EDGE,"E69.MirrorCS"),sQuery(id+"F0.wireOp",EDGE,"E70.MirrorCS")])],"isStart":false}),makeQuery(id+"F4.opExtrude","SWEPT_FACE",FACE,{"disambiguationData":[OSD([sQuery(id+"F3.wireOp",EDGE,"E100.MirrorCS")])]})]});
            var Q19;
            Q19=makeQuery(id+"F4.boolean.opBoolean","INTERSECT",EDGE,{"derivedFrom":[makeQuery(id+"F2.opExtrude","CAP_FACE",FACE,{"disambiguationData":[OSD([sQuery(id+"F0.wireOp",EDGE,"E2"),sQuery(id+"F0.wireOp",EDGE,"E3"),sQuery(id+"F0.wireOp",EDGE,"E4"),sQuery(id+"F0.wireOp",EDGE,"E5"),sQuery(id+"F0.wireOp",EDGE,"E6"),sQuery(id+"F0.wireOp",EDGE,"E7"),sQuery(id+"F0.wireOp",EDGE,"E8"),sQuery(id+"F0.wireOp",EDGE,"E9"),sQuery(id+"F0.wireOp",EDGE,"E10"),sQuery(id+"F0.wireOp",EDGE,"E11"),sQuery(id+"F0.wireOp",EDGE,"E12"),sQuery(id+"F0.wireOp",EDGE,"E13"),sQuery(id+"F0.wireOp",EDGE,"E14"),sQuery(id+"F0.wireOp",EDGE,"E15"),sQuery(id+"F0.wireOp",EDGE,"E16"),sQuery(id+"F0.wireOp",EDGE,"E17"),sQuery(id+"F0.wireOp",EDGE,"E18"),sQuery(id+"F0.wireOp",EDGE,"E19"),sQuery(id+"F0.wireOp",EDGE,"E20"),sQuery(id+"F0.wireOp",EDGE,"E21"),sQuery(id+"F0.wireOp",EDGE,"E22"),sQuery(id+"F0.wireOp",EDGE,"E23"),sQuery(id+"F0.wireOp",EDGE,"E24"),sQuery(id+"F0.wireOp",EDGE,"E25"),sQuery(id+"F0.wireOp",EDGE,"E26"),sQuery(id+"F0.wireOp",EDGE,"E27"),sQuery(id+"F0.wireOp",EDGE,"E28"),sQuery(id+"F0.wireOp",EDGE,"E29"),sQuery(id+"F0.wireOp",EDGE,"E30"),sQuery(id+"F0.wireOp",EDGE,"E31"),sQuery(id+"F0.wireOp",EDGE,"E32"),sQuery(id+"F0.wireOp",EDGE,"E33"),sQuery(id+"F0.wireOp",EDGE,"E34"),sQuery(id+"F0.wireOp",EDGE,"E36"),sQuery(id+"F0.wireOp",EDGE,"E37.MirrorCS"),sQuery(id+"F0.wireOp",EDGE,"E38.MirrorCS"),sQuery(id+"F0.wireOp",EDGE,"E39.MirrorCS"),sQuery(id+"F0.wireOp",EDGE,"E40.MirrorCS"),sQuery(id+"F0.wireOp",EDGE,"E41.MirrorCS"),sQuery(id+"F0.wireOp",EDGE,"E42.MirrorCS"),sQuery(id+"F0.wireOp",EDGE,"E43.MirrorCS"),sQuery(id+"F0.wireOp",EDGE,"E44.MirrorCS"),sQuery(id+"F0.wireOp",EDGE,"E45.MirrorCS"),sQuery(id+"F0.wireOp",EDGE,"E46.MirrorCS"),sQuery(id+"F0.wireOp",EDGE,"E47.MirrorCS"),sQuery(id+"F0.wireOp",EDGE,"E48.MirrorCS"),sQuery(id+"F0.wireOp",EDGE,"E49.MirrorCS"),sQuery(id+"F0.wireOp",EDGE,"E50.MirrorCS"),sQuery(id+"F0.wireOp",EDGE,"E51.MirrorCS"),sQuery(id+"F0.wireOp",EDGE,"E52.MirrorCS"),sQuery(id+"F0.wireOp",EDGE,"E53.MirrorCS"),sQuery(id+"F0.wireOp",EDGE,"E54.MirrorCS"),sQuery(id+"F0.wireOp",EDGE,"E55.MirrorCS"),sQuery(id+"F0.wireOp",EDGE,"E56.MirrorCS"),sQuery(id+"F0.wireOp",EDGE,"E57.MirrorCS"),sQuery(id+"F0.wireOp",EDGE,"E58.MirrorCS"),sQuery(id+"F0.wireOp",EDGE,"E59.MirrorCS"),sQuery(id+"F0.wireOp",EDGE,"E60.MirrorCS"),sQuery(id+"F0.wireOp",EDGE,"E61.MirrorCS"),sQuery(id+"F0.wireOp",EDGE,"E62.MirrorCS"),sQuery(id+"F0.wireOp",EDGE,"E63.MirrorCS"),sQuery(id+"F0.wireOp",EDGE,"E64.MirrorCS"),sQuery(id+"F0.wireOp",EDGE,"E65.MirrorCS"),sQuery(id+"F0.wireOp",EDGE,"E66.MirrorCS"),sQuery(id+"F0.wireOp",EDGE,"E67.MirrorCS"),sQuery(id+"F0.wireOp",EDGE,"E68.MirrorCS"),sQuery(id+"F0.wireOp",EDGE,"E69.MirrorCS"),sQuery(id+"F0.wireOp",EDGE,"E70.MirrorCS")])],"isStart":false}),makeQuery(id+"F4.opExtrude","SWEPT_FACE",FACE,{"disambiguationData":[OSD([sQuery(id+"F3.wireOp",EDGE,"E99.MirrorCS")])]})]});
            chamfer(context, id + "F5", {"entities" : qUnion([Q0, Q1, Q2, Q3, Q4, Q5, Q6, Q7, Q8, Q9, Q10, Q11, Q12, Q13, Q14, Q15, Q16, Q17, Q18, Q19]), "width" : 5.08 * mm, "tangentPropagation" : true});
        }
        {
            var Q0;
            Q0=makeQuery(id+"F2.opExtrude","CAP_EDGE",EDGE,{"disambiguationData":[OSD([sQuery(id+"F0.wireOp",EDGE,"E8")])],"isStart":false});
            var Q1;
            Q1=makeQuery(id+"F2.opExtrude","CAP_EDGE",EDGE,{"disambiguationData":[OSD([sQuery(id+"F0.wireOp",EDGE,"E7")])],"isStart":false});
            var Q2;
            Q2=makeQuery(id+"F2.opExtrude","CAP_EDGE",EDGE,{"disambiguationData":[OSD([sQuery(id+"F0.wireOp",EDGE,"E43.MirrorCS")])],"isStart":false});
            var Q3;
            Q3=makeQuery(id+"F2.opExtrude","CAP_EDGE",EDGE,{"disambiguationData":[OSD([sQuery(id+"F0.wireOp",EDGE,"E45.MirrorCS")])],"isStart":false});
            var Q4;
            Q4=makeQuery(id+"F1.opExtrude","CAP_EDGE",EDGE,{"disambiguationData":[OSD([sQuery(id+"F0.wireOp",EDGE,"E45.MirrorCS")])],"isStart":false});
            var Q5;
            Q5=makeQuery(id+"F1.opExtrude","CAP_EDGE",EDGE,{"disambiguationData":[OSD([sQuery(id+"F0.wireOp",EDGE,"E43.MirrorCS")])],"isStart":false});
            var Q6;
            Q6=makeQuery(id+"F1.opExtrude","CAP_EDGE",EDGE,{"disambiguationData":[OSD([sQuery(id+"F0.wireOp",EDGE,"E8")])],"isStart":false});
            var Q7;
            Q7=makeQuery(id+"F1.opExtrude","CAP_EDGE",EDGE,{"disambiguationData":[OSD([sQuery(id+"F0.wireOp",EDGE,"E7")])],"isStart":false});
            chamfer(context, id + "F6", {"entities" : qUnion([Q0, Q1, Q2, Q3, Q4, Q5, Q6, Q7]), "width" : 2.54 * mm, "tangentPropagation" : true});
        }
    });
